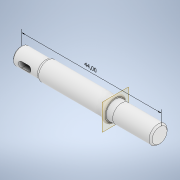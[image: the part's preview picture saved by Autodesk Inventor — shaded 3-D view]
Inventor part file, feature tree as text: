
AUTODESK INVENTOR PART (.ipt)
format: ipt  version: 2022.6 (Build 266554000, 554)  size: 211,456 bytes
history: native  units: mm
features: extrude x5, other x4, plane x2, fillet x2, projected_geometry x2, loft x1, chamfer x1
ambient origin geometry x8: Origin, YZ Plane, XZ Plane, XY Plane, X Axis, Y Axis, Z Axis, Center Point
bodies: Solid1 (feature_tree)
feature tree (17):
  other  "Annotations"
  extrude  "Shaft"  TaperAngle=0.0deg  [1 undecoded]
  extrude  "Slot for Differential Gear"  Depth=2.35mm TaperAngle=0.0deg
  plane  "Work Plane1"
  extrude  "Wheel Insert Profile"  Depth=1.8mm
  loft  "Loft1"
  plane  "Work Plane2"
  extrude  "Stopper"  Depth=1.0mm
  fillet  "Fillet1"  Radius=7.0mm
  extrude  "Differential Gear Insert Profile"  Depth=12.0mm TaperAngle=0.0deg
  fillet  "Fillet3"  Radius=2.0mm
  chamfer  "Chamfer4"  Distance=7.5mm
  projected_geometry  "Projected Loop1"
  other  "Edges2"
  other  "Edges4"
  projected_geometry  "Project Cut Edges1"
  other  "Linear Dimension 1"
note: 1 required parameter value undecoded (feature->parameter linkage not recoverable at this tier; creation-order binding heuristic only, values carry confidence <= 0.55)
